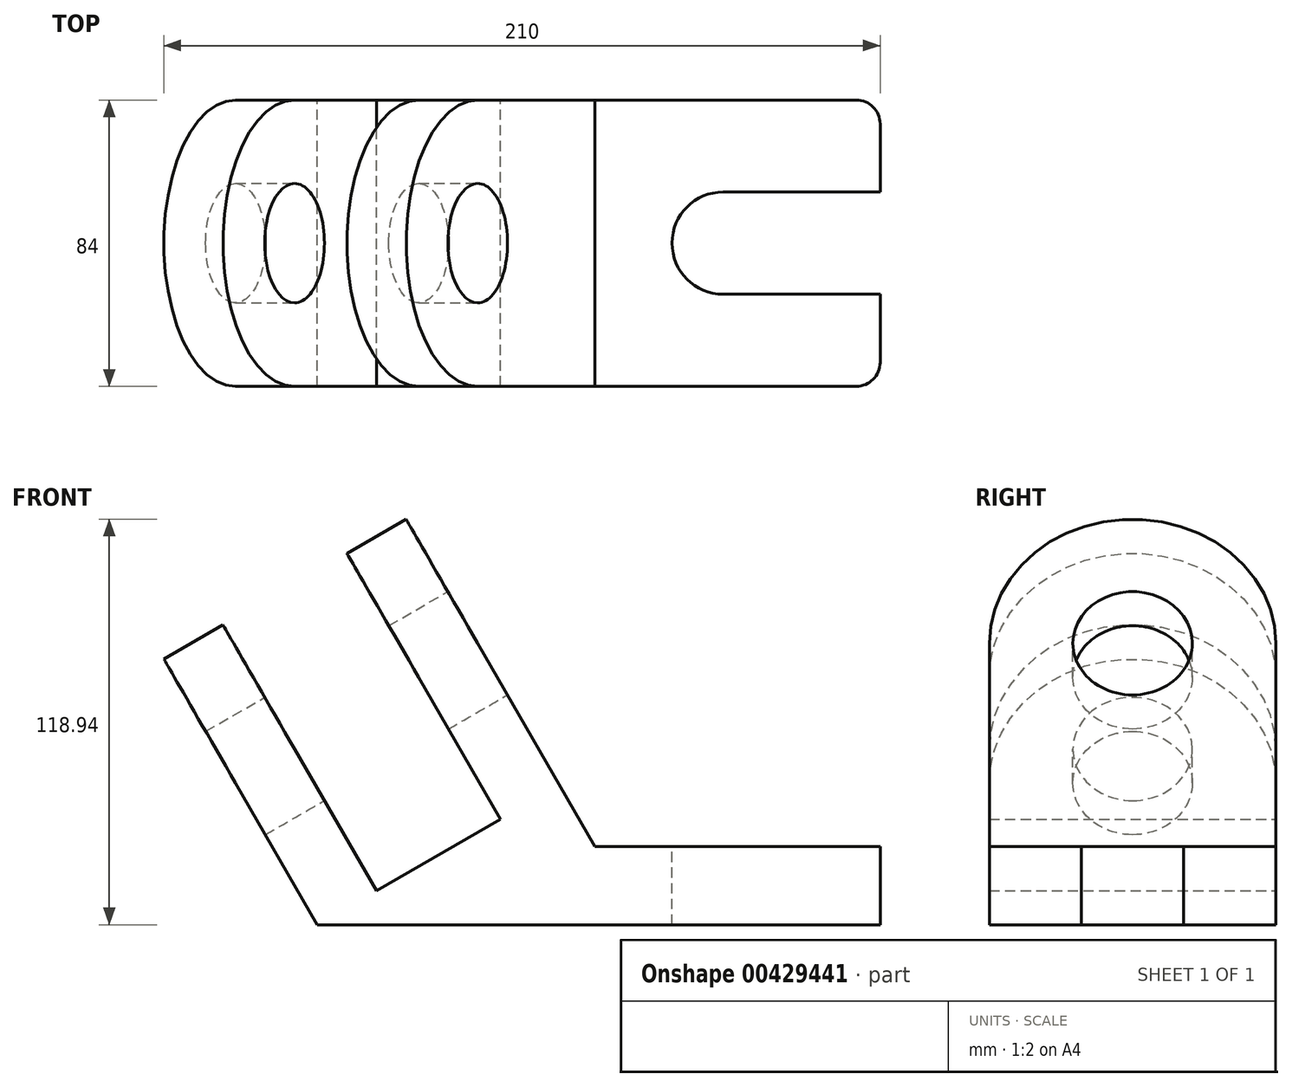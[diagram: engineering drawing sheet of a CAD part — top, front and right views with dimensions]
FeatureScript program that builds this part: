
annotation { "Feature Type Name" : "Feature", "Feature Type Description" : "" }
export const myFeature = defineFeature(function(context is Context, id is Id, definition is map)
    precondition{}
    {
        {
            var Q0;
            Q0=qCreatedBy(makeId("Front.planeOp"),FACE);
            var sketch = newSketch(context, id + "F0", { "sketchPlane" : qUnion([Q0])});
            skLineSegment(sketch, "E0", {"start": v(-36.67, 0) * mm, "end": v(128.33, 0) * mm});
            skLineSegment(sketch, "E1", {"start": v(128.33, 0) * mm, "end": v(128.33, 23) * mm});
            skLineSegment(sketch, "E2", {"start": v(128.33, 23) * mm, "end": v(82.33, 23) * mm});
            skLineSegment(sketch, "E3", {"start": v(-36.67, 0) * mm, "end": v(-81.67, 77.94) * mm});
            skLineSegment(sketch, "E4", {"start": v(-81.67, 77.94) * mm, "end": v(-64.35, 87.94) * mm});
            skLineSegment(sketch, "E5", {"start": v(-64.35, 87.94) * mm, "end": v(-19.35, 10) * mm});
            skLineSegment(sketch, "E6", {"start": v(-19.35, 10) * mm, "end": v(17.02, 31) * mm});
            skLineSegment(sketch, "E7", {"start": v(17.02, 31) * mm, "end": v(-27.98, 108.94) * mm});
            skLineSegment(sketch, "E8", {"start": v(-27.98, 108.94) * mm, "end": v(-10.66, 118.94) * mm});
            skLineSegment(sketch, "E9", {"start": v(-10.66, 118.94) * mm, "end": v(34.34, 41) * mm});
            skLineSegment(sketch, "E10", {"start": v(34.34, 41) * mm, "end": v(44.73, 23) * mm});
            skLineSegment(sketch, "E11", {"start": v(44.73, 23) * mm, "end": v(82.33, 23) * mm});
            skSolve(sketch);
        }
        {
            var Q0;
            Q0 = qSketchRegion(id + "F0", true);
            extrude(context, id + "F1", {"entities" : qUnion([Q0]), "depth" : 84 * mm});
        }
        {
            var Q0;
            Q0=makeQuery(id+"F1.opExtrude","SWEPT_FACE",FACE,{"disambiguationData":[OSD([sQuery(id+"F0.wireOp",EDGE,"E2"),sQuery(id+"F0.wireOp",EDGE,"E11")])]});
            var sketch = newSketch(context, id + "F2", { "sketchPlane" : qUnion([Q0])});
            skArc(sketch, "E12", {"start": v(82.33, -27) * mm, "mid": v(67.33, -42) * mm, "end": v(82.33, -57) * mm});
            skLineSegment(sketch, "E13", {"start": v(82.33, -27) * mm, "end": v(128.33, -27) * mm});
            skLineSegment(sketch, "E14", {"start": v(128.33, -57) * mm, "end": v(82.33, -57) * mm});
            skSolve(sketch);
        }
        {
            var Q0;
            Q0=makeQuery(id+"F2.imprint","IMPRINT",FACE,{"disambiguationData":[TD([[makeQuery(id+"F2.imprint","IMPRINT",EDGE,{"derivedFrom":sQuery(id+"F2.wireOp",EDGE,"E12")}),1.0]])]});
            extrude(context, id + "F3", {"entities" : qUnion([Q0]), "operationType" : NewBodyOperationType.REMOVE, "oppositeDirection" : true, "depth" : 25 * mm});
        }
        {
            var Q0;
            Q0=makeQuery(id+"F1.opExtrude","CAP_EDGE",EDGE,{"disambiguationData":[OSD([sQuery(id+"F0.wireOp",EDGE,"E1")])],"isStart":true});
            var Q1;
            Q1=makeQuery(id+"F1.opExtrude","CAP_EDGE",EDGE,{"disambiguationData":[OSD([sQuery(id+"F0.wireOp",EDGE,"E1")])],"isStart":false});
            fillet(context, id + "F4", {"entities" : qUnion([Q0, Q1]), "radius" : 7 * mm, "tangentPropagation" : true, "allowEdgeOverflow" : false});
        }
        {
            var Q0;
            Q0=makeQuery(id+"F1.opExtrude","SWEPT_FACE",FACE,{"disambiguationData":[OSD([sQuery(id+"F0.wireOp",EDGE,"E9"),sQuery(id+"F0.wireOp",EDGE,"E10")])]});
            var sketch = newSketch(context, id + "F5", { "sketchPlane" : qUnion([Q0])});
            skCircle(sketch, "E15", {"center": v(-42, 66.34) * mm, "radius": 17.5 * mm});
            skCircle(sketch, "E16", {"center": v(-42, 66.34) * mm, "radius": 42 * mm});
            skSolve(sketch);
        }
        {
            var Q0;
            Q0=makeQuery(id+"F5.imprint","IMPRINT",FACE,{"disambiguationData":[TD([[makeQuery(id+"F5.imprint","IMPRINT",EDGE,{"derivedFrom":sQuery(id+"F5.wireOp",EDGE,"E15")}),1.0]])]});
            var Q1;
            {var subQ0=sQuery(id+"F5.wireOp",EDGE,"E16");var subQ1=sQuery(id+"F0.wireOp",EDGE,"E9");var subQ2=makeQuery(id+"F1.opExtrude","SWEPT_EDGE",EDGE,{"disambiguationData":[OSD([sQuery(id+"F0.wireOp",EDGE,"E8"),subQ1])]});var subQ3=makeQuery(id+"F5.imprint","INTERSECT",VERTEX,{"derivedFrom":[subQ2,subQ0]});Q1=makeQuery(id+"F5.imprint","IMPRINT",FACE,{"disambiguationData":[TD([[makeQuery(id+"F5.imprint","IMPRINT",EDGE,{"disambiguationData":[TD([[subQ3,-1.0]])],"derivedFrom":subQ0}),-1.0]])]});}
            var Q2;
            {var subQ0=sQuery(id+"F5.wireOp",EDGE,"E16");var subQ1=sQuery(id+"F0.wireOp",EDGE,"E9");var subQ2=makeQuery(id+"F1.opExtrude","SWEPT_EDGE",EDGE,{"disambiguationData":[OSD([sQuery(id+"F0.wireOp",EDGE,"E8"),subQ1])]});var subQ3=makeQuery(id+"F5.imprint","INTERSECT",VERTEX,{"derivedFrom":[subQ2,subQ0]});Q2=makeQuery(id+"F5.imprint","IMPRINT",FACE,{"disambiguationData":[TD([[makeQuery(id+"F5.imprint","IMPRINT",EDGE,{"disambiguationData":[TD([[subQ3,1.0]])],"derivedFrom":subQ0}),-1.0]])]});}
            extrude(context, id + "F6", {"entities" : qUnion([Q0, Q1, Q2]), "operationType" : NewBodyOperationType.REMOVE, "oppositeDirection" : true, "depth" : 100 * mm});
        }
    });
